# Revit family: Toilet-Round-American_Standard-Studio-2795.204.020
name_source: partatom
category: Plumbing Fixtures
units: mm (PartAtom-declared; Revit-internal decimal feet)

## family parameters
Always vertical = No
Cut with Voids When Loaded = No
OmniClass Number = 23.45.05.21.11.11
OmniClass Title = Water Operated Water Closets
Part Type = Normal
Room Calculation Point = No
Round Connector Dimension = Use Radius
Shared = Yes
Work Plane-Based = Yes

## types (1)
- 2795.204.020
    Assembly Code = D2010110
    Bowl Shape = Round Front
    CW Connection = Yes
    CWFU = 5
    Cold Water Connection Diameter = 1/2"
    Cold Water Connection Height = 5 1/2"
    Cold Water Connection Radius = 1/4"
    Cold Water Connection Width = 8"
    Default Elevation = 0"
    Description = Studio® Concealed Trapway Dual Flush Right Height® Round Front Toilet With Seat
    Finish = Vitreous China-American Standard-020-White
    Flush Rate = 1.6 gpf (6.0Lpf)/1.1 gpf(4.1Lpf)
    HW Connection = No
    HWFU = 0
    Height = 30 7/8"
    Installation Type = Floor Mounted
    Length = 28 1/4"
    Manufacturer = American Standard
    Material = Vitreous China-American Standard-020-White
    Model = 2795.204.020
    Price = Prices may vary. Please consult Manufacturer Representative for most up-to-date price list.
    Product Documentation Link = https://www.americanstandard-us.com
    Product Page URL = https://www.americanstandard-us.com
    Revised Date = 03/16/2021
    Supply Position 1 (8") = Yes
    Supply Position 2 (2-1/4") = No
    URL = https://www.americanstandard-us.com
    Vent Connection = No
    WFU = 5
    Warranty Information = 5 year warranty on entire toilet
    Waste Connection = Yes
    Waste Connection Diameter = 2 1/8"
    Waste Connection Radius = 1 1/16"
    Width = 15 3/4"

## geometry (parser evidence)
native form markers: Sweep x2
no freeform markers — native parametric forms only
